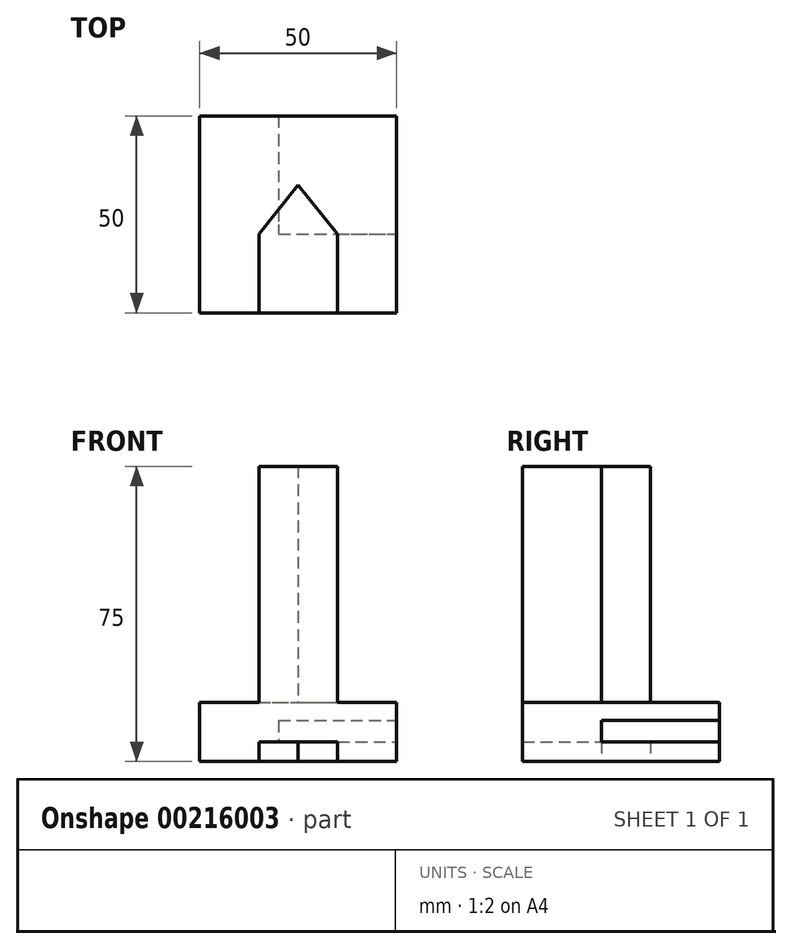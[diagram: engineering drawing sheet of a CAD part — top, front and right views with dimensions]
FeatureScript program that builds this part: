
annotation { "Feature Type Name" : "Feature", "Feature Type Description" : "" }
export const myFeature = defineFeature(function(context is Context, id is Id, definition is map)
    precondition{}
    {
        {
            var Q0;
            Q0=qCreatedBy(makeId("Top.planeOp"),FACE);
            var sketch = newSketch(context, id + "F0", { "sketchPlane" : qUnion([Q0])});
            skLineSegment(sketch, "E0.bottom", {"start": v(0, 0) * mm, "end": v(50, 0) * mm});
            skLineSegment(sketch, "E0.top", {"start": v(0, -50) * mm, "end": v(50, -50) * mm});
            skLineSegment(sketch, "E0.left", {"start": v(0, 0) * mm, "end": v(0, -50) * mm});
            skLineSegment(sketch, "E0.right", {"start": v(50, 0) * mm, "end": v(50, -50) * mm});
            skSolve(sketch);
        }
        {
            var Q0;
            Q0=makeQuery(id+"F0.imprint","IMPRINT",FACE,{"disambiguationData":[TD([[makeQuery(id+"F0.imprint","IMPRINT",EDGE,{"derivedFrom":sQuery(id+"F0.wireOp",EDGE,"E0.bottom")}),-1.0]])]});
            extrude(context, id + "F1", {"entities" : qUnion([Q0]), "depth" : 15 * mm});
        }
        {
            var Q0;
            Q0=makeQuery(id+"F1.opExtrude","CAP_FACE",FACE,{"disambiguationData":[OSD([sQuery(id+"F0.wireOp",EDGE,"E0.bottom"),sQuery(id+"F0.wireOp",EDGE,"E0.top"),sQuery(id+"F0.wireOp",EDGE,"E0.left"),sQuery(id+"F0.wireOp",EDGE,"E0.right")])],"isStart":false});
            var sketch = newSketch(context, id + "F2", { "sketchPlane" : qUnion([Q0])});
            skLineSegment(sketch, "E1.bottom", {"start": v(15, -50) * mm, "end": v(35, -50) * mm});
            skLineSegment(sketch, "E1.left", {"start": v(15, -50) * mm, "end": v(15, -30) * mm});
            skLineSegment(sketch, "E1.right", {"start": v(35, -50) * mm, "end": v(35, -30) * mm});
            skLineSegment(sketch, "E2", {"start": v(15, -30) * mm, "end": v(25, -17.51) * mm});
            skLineSegment(sketch, "E3", {"start": v(25, -17.51) * mm, "end": v(35, -30) * mm});
            skSolve(sketch);
        }
        {
            var Q0;
            Q0 = qSketchRegion(id + "F2", true);
            extrude(context, id + "F3", {"entities" : qUnion([Q0]), "operationType" : NewBodyOperationType.ADD, "offsetDistance" : 25 * mm, "depth" : 60 * mm});
        }
        {
            var Q0;
            Q0=makeQuery(id+"F1.opExtrude","CAP_FACE",FACE,{"disambiguationData":[OSD([sQuery(id+"F0.wireOp",EDGE,"E0.bottom"),sQuery(id+"F0.wireOp",EDGE,"E0.top"),sQuery(id+"F0.wireOp",EDGE,"E0.left"),sQuery(id+"F0.wireOp",EDGE,"E0.right")])],"isStart":true});
            var sketch = newSketch(context, id + "F4", { "sketchPlane" : qUnion([Q0])});
            skLineSegment(sketch, "E4.bottom", {"start": v(15, 50) * mm, "end": v(35, 50) * mm});
            skLineSegment(sketch, "E4.left", {"start": v(15, 50) * mm, "end": v(15, 30) * mm});
            skLineSegment(sketch, "E4.right", {"start": v(35, 50) * mm, "end": v(35, 30) * mm});
            skLineSegment(sketch, "E5", {"start": v(35, 30) * mm, "end": v(25, 17.51) * mm});
            skLineSegment(sketch, "E6", {"start": v(25, 17.51) * mm, "end": v(15, 30) * mm});
            skSolve(sketch);
        }
        {
            var Q0;
            Q0 = qSketchRegion(id + "F4", true);
            extrude(context, id + "F5", {"entities" : qUnion([Q0]), "operationType" : NewBodyOperationType.REMOVE, "oppositeDirection" : true, "offsetDistance" : 25 * mm, "depth" : 5 * mm});
        }
        {
            var Q0;
            Q0=makeQuery(id+"F1.opExtrude","SWEPT_FACE",FACE,{"disambiguationData":[OSD([sQuery(id+"F0.wireOp",EDGE,"E0.right")])]});
            var sketch = newSketch(context, id + "F6", { "sketchPlane" : qUnion([Q0])});
            skLineSegment(sketch, "E7.bottom", {"start": v(0, 10.4) * mm, "end": v(-30, 10.4) * mm});
            skLineSegment(sketch, "E7.top", {"start": v(0, 5) * mm, "end": v(-30, 5) * mm});
            skLineSegment(sketch, "E7.left", {"start": v(0, 10.4) * mm, "end": v(0, 5) * mm});
            skLineSegment(sketch, "E7.right", {"start": v(-30, 10.4) * mm, "end": v(-30, 5) * mm});
            skSolve(sketch);
        }
        {
            var Q0;
            Q0 = qSketchRegion(id + "F6", true);
            extrude(context, id + "F7", {"entities" : qUnion([Q0]), "operationType" : NewBodyOperationType.REMOVE, "oppositeDirection" : true, "depth" : 30 * mm});
        }
    });
